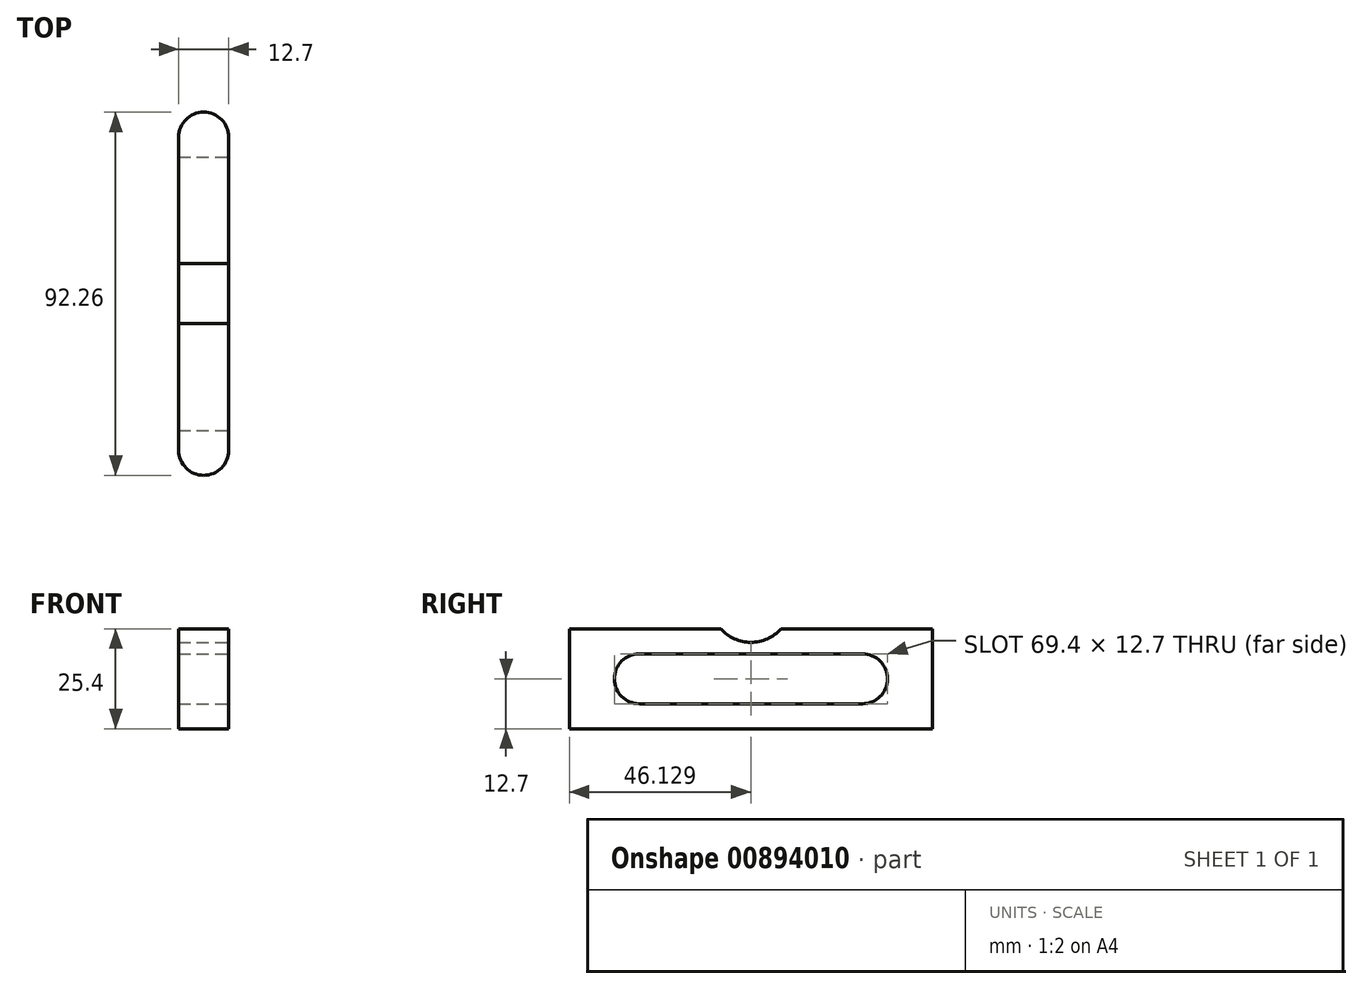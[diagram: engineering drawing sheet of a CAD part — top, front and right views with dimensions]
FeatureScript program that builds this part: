
annotation { "Feature Type Name" : "Feature", "Feature Type Description" : "" }
export const myFeature = defineFeature(function(context is Context, id is Id, definition is map)
    precondition{}
    {
        {
            var Q0;
            Q0=qCreatedBy(makeId("Top.planeOp"),FACE);
            var sketch = newSketch(context, id + "F0", { "sketchPlane" : qUnion([Q0])});
            skArc(sketch, "E0", {"start": v(-34.66, -46.57) * mm, "mid": v(-28.31, -52.92) * mm, "end": v(-21.96, -46.57) * mm});
            skArc(sketch, "E1", {"start": v(-21.96, 32.99) * mm, "mid": v(-28.31, 39.34) * mm, "end": v(-34.66, 32.99) * mm});
            skLineSegment(sketch, "E2", {"start": v(-34.66, 32.99) * mm, "end": v(-34.66, -46.57) * mm});
            skLineSegment(sketch, "E3", {"start": v(-21.96, 32.99) * mm, "end": v(-21.96, -46.57) * mm});
            skSolve(sketch);
        }
        {
            var Q0;
            Q0 = qSketchRegion(id + "F0", true);
            extrude(context, id + "F1", {"entities" : qUnion([Q0]), "depth" : 25.4 * mm, "offsetDistance" : 25.4 * mm});
        }
        {
            var Q0;
            Q0=makeQuery(id+"F1.opExtrude","SWEPT_FACE",FACE,{"disambiguationData":[OSD([sQuery(id+"F0.wireOp",EDGE,"E3")])]});
            var sketch = newSketch(context, id + "F2", { "sketchPlane" : qUnion([Q0])});
            skArc(sketch, "E4", {"start": v(-35.14, 19.05) * mm, "mid": v(-41.49, 12.7) * mm, "end": v(-35.14, 6.35) * mm});
            skArc(sketch, "E5", {"start": v(21.56, 6.35) * mm, "mid": v(27.9, 12.7) * mm, "end": v(21.56, 19.05) * mm});
            skLineSegment(sketch, "E6", {"start": v(-35.14, 19.05) * mm, "end": v(21.56, 19.05) * mm});
            skLineSegment(sketch, "E7", {"start": v(-35.14, 6.35) * mm, "end": v(21.56, 6.35) * mm});
            skPoint(sketch, "E8.start.orphan", {"position": v(-46.57, 12.7) * mm});
            skPoint(sketch, "E9.trimOffspring.end.orphan", {"position": v(32.99, 12.7) * mm});
            skSolve(sketch);
        }
        {
            var Q0;
            Q0 = qSketchRegion(id + "F2", true);
            extrude(context, id + "F3", {"entities" : qUnion([Q0]), "operationType" : NewBodyOperationType.REMOVE, "oppositeDirection" : true, "depth" : 25.4 * mm, "offsetDistance" : 25.4 * mm});
        }
        {
            var Q0;
            Q0=makeQuery(id+"F1.opExtrude","SWEPT_FACE",FACE,{"disambiguationData":[OSD([sQuery(id+"F0.wireOp",EDGE,"E3")])]});
            var sketch = newSketch(context, id + "F4", { "sketchPlane" : qUnion([Q0])});
            skLineSegment(sketch, "E10", {"start": v(-6.8, 25.4) * mm, "end": v(-6.8, 19.05) * mm});
            skLineSegment(sketch, "E11", {"start": v(-6.8, 25.4) * mm, "end": v(-14.41, 25.4) * mm});
            skLineSegment(sketch, "E12", {"start": v(-6.8, 25.4) * mm, "end": v(0.83, 25.4) * mm});
            skArc(sketch, "E13", {"start": v(-14.41, 25.4) * mm, "mid": v(-6.8, 21.96) * mm, "end": v(0.83, 25.4) * mm});
            skLineSegment(sketch, "E14", {"start": v(-14.41, 25.4) * mm, "end": v(0.83, 25.4) * mm});
            skSolve(sketch);
        }
        {
            var Q0;
            Q0 = qSketchRegion(id + "F4", true);
            extrude(context, id + "F5", {"entities" : qUnion([Q0]), "operationType" : NewBodyOperationType.REMOVE, "oppositeDirection" : true, "depth" : 25.4 * mm, "offsetDistance" : 25.4 * mm});
        }
    });
